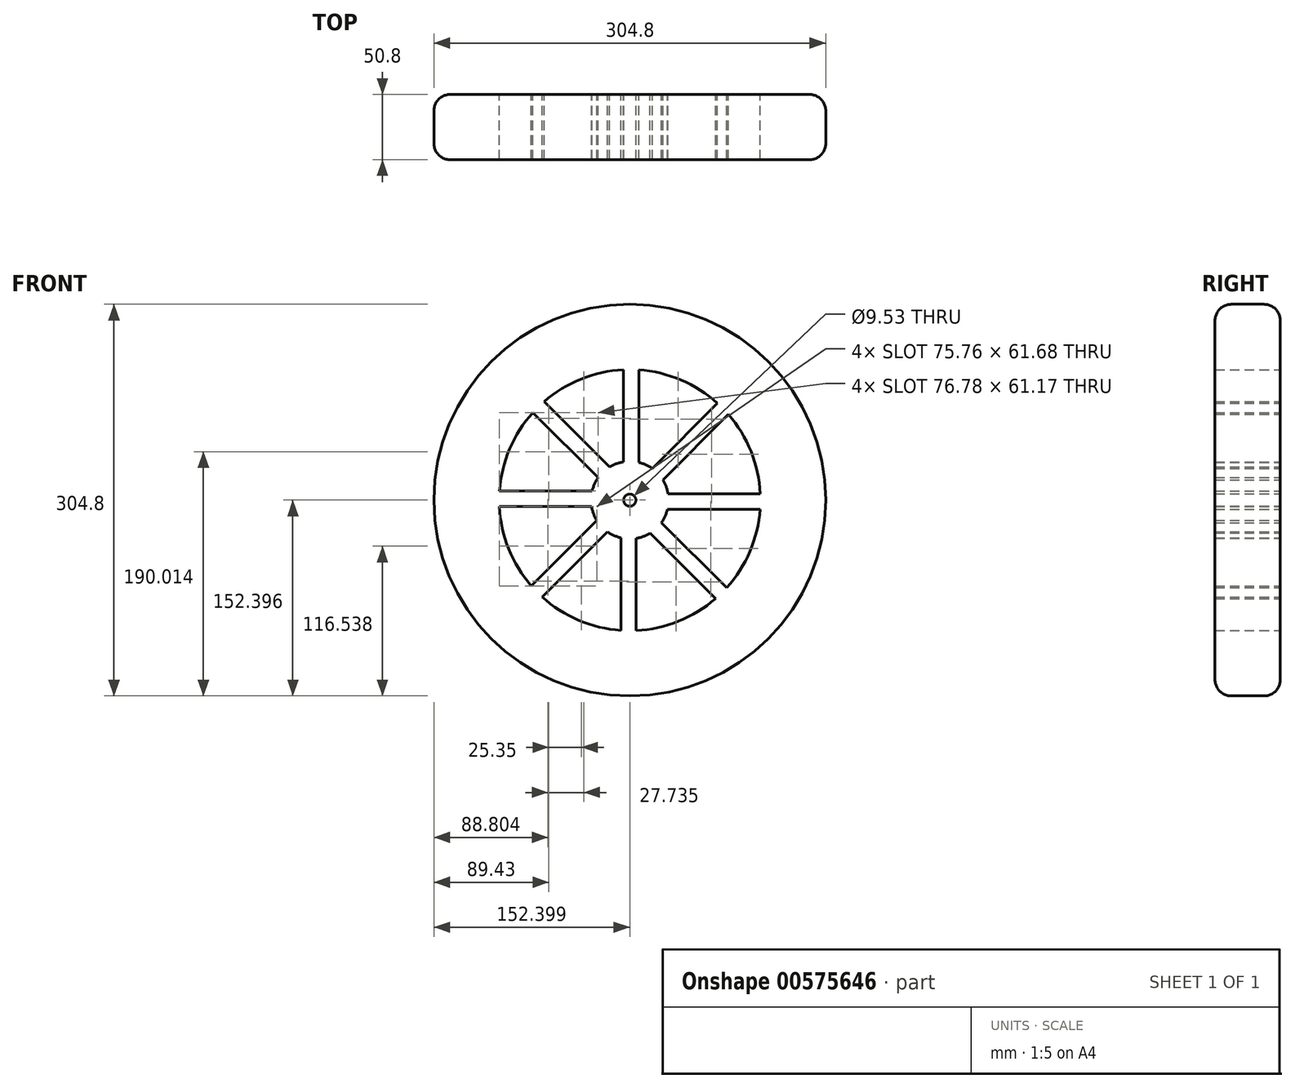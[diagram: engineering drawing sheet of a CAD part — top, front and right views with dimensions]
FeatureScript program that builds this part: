
annotation { "Feature Type Name" : "Feature", "Feature Type Description" : "" }
export const myFeature = defineFeature(function(context is Context, id is Id, definition is map)
    precondition{}
    {
        {
            var Q0;
            Q0=qCreatedBy(makeId("Front.planeOp"),FACE);
            var sketch = newSketch(context, id + "F0", { "sketchPlane" : qUnion([Q0])});
            skCircle(sketch, "E0", {"center": v(-53.95, 5.73) * mm, "radius": 152.4 * mm});
            skCircle(sketch, "E1", {"center": v(-53.95, 5.73) * mm, "radius": 4.76 * mm});
            skArc(sketch, "E2.0", {"start": v(-58.97, 107.2) * mm, "mid": v(-91.9, 99.97) * mm, "end": v(-120.65, 82.37) * mm});
            skArc(sketch, "E3.0", {"start": v(-36.47, 30.3) * mm, "mid": v(-41.47, 33.18) * mm, "end": v(-46.92, 35.06) * mm});
            skLineSegment(sketch, "E4.0", {"start": v(-46.92, 18.34) * mm, "end": v(-46.92, 19.86) * mm});
            skLineSegment(sketch, "E5.0", {"start": v(-58.97, 18.58) * mm, "end": v(-58.97, 20.69) * mm});
            skLineSegment(sketch, "E6.1.0", {"start": v(-57.9, 19.61) * mm, "end": v(-58.97, 20.69) * mm});
            skLineSegment(sketch, "E6.1.1", {"start": v(-66.59, 11.26) * mm, "end": v(-68.08, 12.76) * mm});
            skLineSegment(sketch, "E6.2.0", {"start": v(-66.56, 12.76) * mm, "end": v(-68.08, 12.76) * mm});
            skLineSegment(sketch, "E6.2.1", {"start": v(-66.8, 0.7) * mm, "end": v(-68.91, 0.7) * mm});
            skLineSegment(sketch, "E6.3.0", {"start": v(-67.84, 1.78) * mm, "end": v(-68.91, 0.7) * mm});
            skLineSegment(sketch, "E6.3.1", {"start": v(-59.49, -6.9) * mm, "end": v(-60.98, -8.4) * mm});
            skLineSegment(sketch, "E6.4.0", {"start": v(-60.98, -6.88) * mm, "end": v(-60.98, -8.4) * mm});
            skLineSegment(sketch, "E6.4.1", {"start": v(-48.93, -7.12) * mm, "end": v(-48.93, -9.24) * mm});
            skLineSegment(sketch, "E6.5.0", {"start": v(-50, -8.16) * mm, "end": v(-48.93, -9.24) * mm});
            skLineSegment(sketch, "E6.5.1", {"start": v(-41.32, 0.2) * mm, "end": v(-39.82, -1.3) * mm});
            skLineSegment(sketch, "E6.6.0", {"start": v(-41.34, -1.3) * mm, "end": v(-39.82, -1.3) * mm});
            skLineSegment(sketch, "E6.6.1", {"start": v(-41.1, 10.75) * mm, "end": v(-38.99, 10.75) * mm});
            skLineSegment(sketch, "E6.7.0", {"start": v(-40.06, 9.67) * mm, "end": v(-38.99, 10.75) * mm});
            skLineSegment(sketch, "E6.7.1", {"start": v(-48.41, 18.36) * mm, "end": v(-46.92, 19.86) * mm});
            skLineSegment(sketch, "E7.trimOffspring", {"start": v(-36.47, 30.3) * mm, "end": v(14.45, 81.22) * mm});
            skLineSegment(sketch, "E8.trimOffspring", {"start": v(-28.24, 21.5) * mm, "end": v(22.8, 72.53) * mm});
            skLineSegment(sketch, "E9.trimOffspring", {"start": v(-46.92, 35.06) * mm, "end": v(-46.92, 107.24) * mm});
            skLineSegment(sketch, "E10.trimOffspring", {"start": v(-58.97, 35.47) * mm, "end": v(-58.97, 107.48) * mm});
            skLineSegment(sketch, "E11.trimOffspring", {"start": v(-69.72, 31.44) * mm, "end": v(-120.76, 82.48) * mm});
            skLineSegment(sketch, "E12.trimOffspring", {"start": v(-83.28, 12.76) * mm, "end": v(-155.46, 12.76) * mm});
            skLineSegment(sketch, "E13.trimOffspring", {"start": v(-78.53, 23.2) * mm, "end": v(-129.45, 74.12) * mm});
            skArc(sketch, "E14.trimOffspring", {"start": v(-78.53, 23.2) * mm, "mid": v(-81.4, 18.21) * mm, "end": v(-83.28, 12.76) * mm});
            skArc(sketch, "E15.trimOffspring", {"start": v(-58.97, 35.47) * mm, "mid": v(-64.54, 33.97) * mm, "end": v(-69.72, 31.44) * mm});
            skArc(sketch, "E16.trimOffspring", {"start": v(-83.7, 0.7) * mm, "mid": v(-82.2, -4.86) * mm, "end": v(-79.66, -10.04) * mm});
            skLineSegment(sketch, "E17.trimOffspring", {"start": v(-83.7, 0.7) * mm, "end": v(-155.7, 0.7) * mm});
            skLineSegment(sketch, "E18.trimOffspring", {"start": v(-79.66, -10.04) * mm, "end": v(-130.7, -61.08) * mm});
            skLineSegment(sketch, "E19.trimOffspring", {"start": v(-71.43, -18.85) * mm, "end": v(-122.35, -69.77) * mm});
            skArc(sketch, "E20.trimOffspring", {"start": v(-71.43, -18.85) * mm, "mid": v(-66.44, -21.73) * mm, "end": v(-60.98, -23.6) * mm});
            skLineSegment(sketch, "E21.trimOffspring", {"start": v(-60.98, -23.6) * mm, "end": v(-60.98, -95.78) * mm});
            skArc(sketch, "E22.trimOffspring", {"start": v(-48.93, -24.02) * mm, "mid": v(-43.36, -22.52) * mm, "end": v(-38.18, -19.99) * mm});
            skLineSegment(sketch, "E23.trimOffspring", {"start": v(-48.93, -24.02) * mm, "end": v(-48.93, -96.02) * mm});
            skLineSegment(sketch, "E24.trimOffspring", {"start": v(-38.18, -19.99) * mm, "end": v(12.86, -71.02) * mm});
            skLineSegment(sketch, "E25.trimOffspring", {"start": v(-29.37, -11.76) * mm, "end": v(21.54, -62.67) * mm});
            skLineSegment(sketch, "E26.trimOffspring", {"start": v(-24.62, -1.3) * mm, "end": v(47.56, -1.3) * mm});
            skLineSegment(sketch, "E27.trimOffspring", {"start": v(-24.2, 10.75) * mm, "end": v(47.8, 10.75) * mm});
            skArc(sketch, "E28.trimOffspring", {"start": v(-24.2, 10.75) * mm, "mid": v(-25.7, 16.31) * mm, "end": v(-28.24, 21.5) * mm});
            skArc(sketch, "E29.trimOffspring", {"start": v(-29.37, -11.76) * mm, "mid": v(-26.5, -6.76) * mm, "end": v(-24.62, -1.3) * mm});
            skArc(sketch, "E30.trimOffspring", {"start": v(-129.25, 73.93) * mm, "mid": v(-147.43, 45.54) * mm, "end": v(-155.3, 12.76) * mm});
            skArc(sketch, "E31.trimOffspring", {"start": v(-155.43, 0.7) * mm, "mid": v(-148.2, -32.22) * mm, "end": v(-130.6, -60.97) * mm});
            skArc(sketch, "E32.trimOffspring", {"start": v(14.25, 81.03) * mm, "mid": v(-14.14, 99.2) * mm, "end": v(-46.92, 107.08) * mm});
            skArc(sketch, "E33.trimOffspring", {"start": v(47.52, 10.75) * mm, "mid": v(40.3, 43.67) * mm, "end": v(22.69, 72.42) * mm});
            skArc(sketch, "E34.trimOffspring", {"start": v(21.35, -62.48) * mm, "mid": v(39.52, -34.08) * mm, "end": v(47.4, -1.3) * mm});
            skArc(sketch, "E35.trimOffspring", {"start": v(-48.93, -95.75) * mm, "mid": v(-16, -88.52) * mm, "end": v(12.75, -70.91) * mm});
            skArc(sketch, "E36.trimOffspring", {"start": v(-122.16, -69.58) * mm, "mid": v(-93.76, -87.75) * mm, "end": v(-60.98, -95.63) * mm});
            skSolve(sketch);
        }
        {
            var Q0;
            Q0=qSketchRegion(id+"F0",true);
            extrude(context, id + "F1", {"entities" : qUnion([Q0]), "depth" : 50.8 * mm, "offsetDistance" : 25.4 * mm});
        }
        {
            var Q0;
            Q0=makeQuery(id+"F1.opExtrude","CAP_EDGE",EDGE,{"disambiguationData":[OSD([sQuery(id+"F0.wireOp",EDGE,"E0")])],"isStart":false});
            var Q1;
            Q1=makeQuery(id+"F1.opExtrude","CAP_EDGE",EDGE,{"disambiguationData":[OSD([sQuery(id+"F0.wireOp",EDGE,"E0")])],"isStart":true});
            fillet(context, id + "F2", {"entities" : qUnion([Q0, Q1]), "radius" : 12.7 * mm, "tangentPropagation" : true, "allowEdgeOverflow" : false});
        }
    });
